# Revit family: P350171-031
name_source: partatom
category: Lighting Fixtures
revit_build: Autodesk Revit 2014 (Build: 20130308_1515(x64)
units: mm (PartAtom-declared; Revit-internal decimal feet)

## types (1)
- P350171-031
    Apparent Load = 60 VA
    Assembly Code = D5020200
    Color Filter = 16777215
    Connector Description = Lighting Connector
    Default Elevation = 48 "
    Description = Stick with simple geometric forms and clean crisp lines with this modern
flush mount. A beautiful opal glass shade visually calms the sharp edges of
the boxy frame in a masterful stroke of design excellence. The frame is coated
in a classic black finish that contrasts the light shade. The light fixture is just
right for spaces in need of a subtle, feminine touch.
    Dimming Lamp Color Temperature Shift = <None>
    Features = A beautiful opal glass shade visually calms the sharp edges of the boxy frame in a masterful
stroke of design excellence.
• The frame is coated in a classic black finish that contrasts the light shade.
• The light fixtures is just right for spaces in need of a subtle, feminine touch.
• Ideal for any foyer, hallway, dining room, or kitchen.
• Perfect for transitional, modern, and contemporary settings.
• Measures 15-3/8-inch width by 5-1/2-inch height.
• Uses two medium base bulbs that are sold separately (60w max - LED or incandescent).
• Able to be fully dimmable with dimmable bulbs.
• Includes installation instructions and mounting hardware.
• Progress Lighting products are designed for exceptional quality, reliability, and functionality.
    Fixture distribution = Direct
    Glass = Paint - Hubbell - White Texture
    Height = 5.5 "
    Housing Material = Paint - Hubbell - Textured Camera Black
    Lamp = LED
    Load Classification = Lighting
    Manufacturer = Progress Lighting
    Model = P350171-031
    Photometric Web File = generic.ies
    Power Factor = 1
    Product Documentation Link = https://hubbellcdn.com
    Product Link = https://www.hubbell.com
    Square = 15.38 "
    Tilt Angle = -90.00°
    URL = https://www.hubbell.com
    Voltage = 120 V
    Warranty = 5 years Warranty
    Wattage Comments = 60W
    Watts = 60 W

## geometry (parser evidence)
native form markers: Sweep x4
no freeform markers — native parametric forms only
